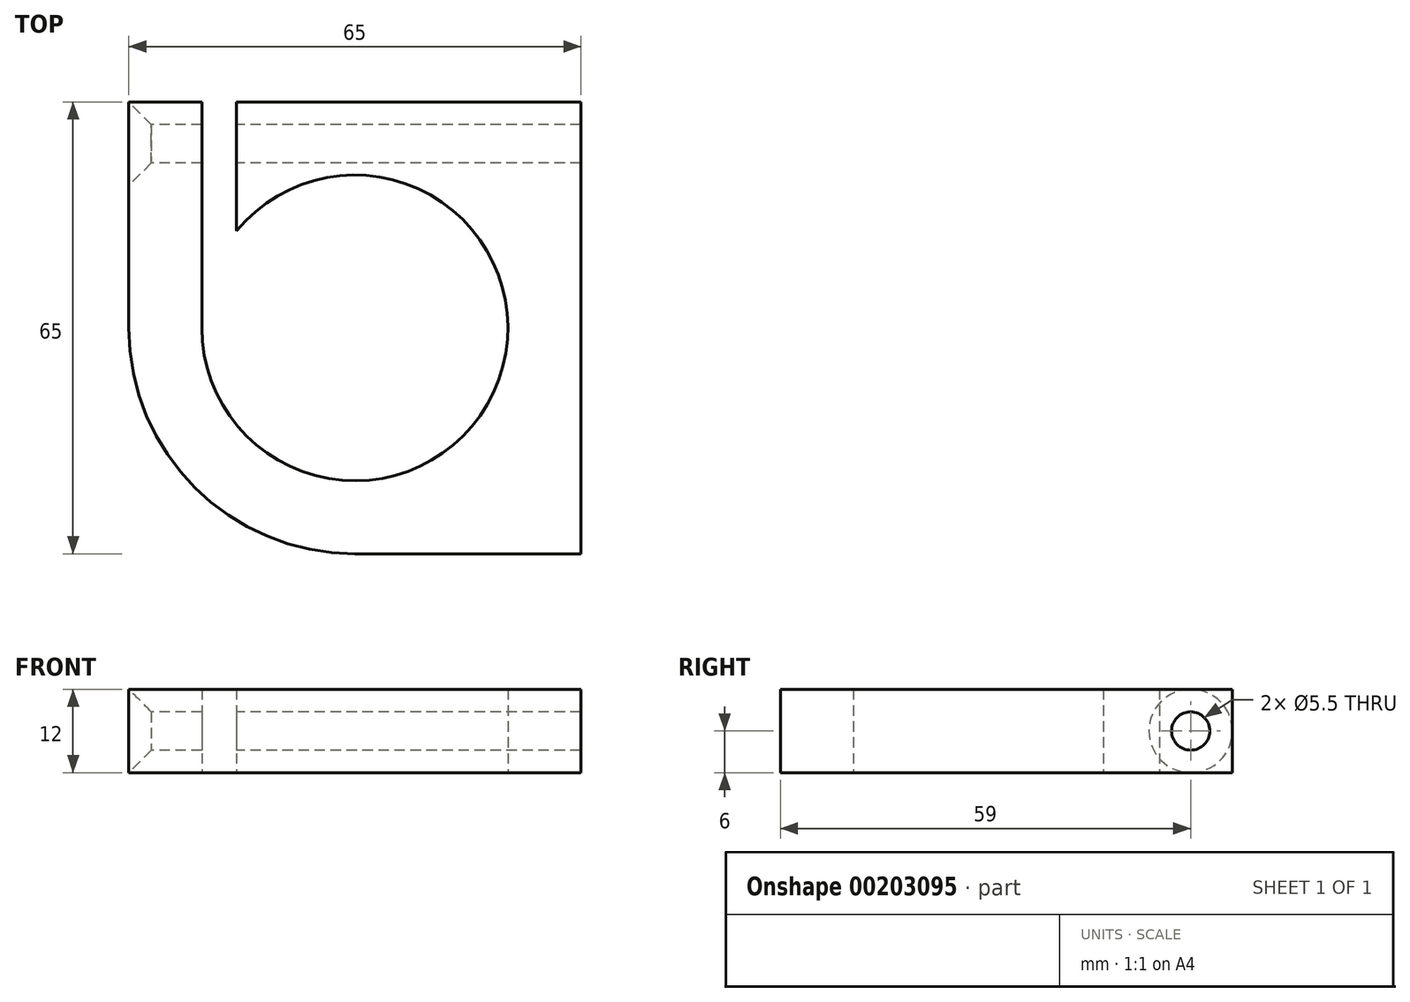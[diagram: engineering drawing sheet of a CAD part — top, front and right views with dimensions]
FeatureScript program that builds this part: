
annotation { "Feature Type Name" : "Feature", "Feature Type Description" : "" }
export const myFeature = defineFeature(function(context is Context, id is Id, definition is map)
    precondition{}
    {
        {
            var Q0;
            Q0=qCreatedBy(makeId("Top.planeOp"),FACE);
            var sketch = newSketch(context, id + "F0", { "sketchPlane" : qUnion([Q0])});
            skArc(sketch, "E0", {"start": v(-22, 0) * mm, "mid": v(20.71, -7.42) * mm, "end": v(-17, 13.96) * mm});
            skArc(sketch, "E1", {"start": v(-32.5, 0) * mm, "mid": v(-22.98, -22.98) * mm, "end": v(0, -32.5) * mm});
            skLineSegment(sketch, "E2", {"start": v(0, -32.5) * mm, "end": v(32.5, -32.5) * mm});
            skLineSegment(sketch, "E3", {"start": v(0, 32.5) * mm, "end": v(32.5, 32.5) * mm});
            skLineSegment(sketch, "E4", {"start": v(32.5, 32.5) * mm, "end": v(32.5, -32.5) * mm});
            skLineSegment(sketch, "E5", {"start": v(0, 32.5) * mm, "end": v(-17, 32.5) * mm});
            skLineSegment(sketch, "E6", {"start": v(-32.5, 0) * mm, "end": v(-32.5, 32.5) * mm});
            skLineSegment(sketch, "E7", {"start": v(-22, 0) * mm, "end": v(-22, 32.5) * mm});
            skLineSegment(sketch, "E8", {"start": v(-17, 13.96) * mm, "end": v(-17, 32.5) * mm});
            skLineSegment(sketch, "E9.trimOffspring", {"start": v(-22, 32.5) * mm, "end": v(-32.5, 32.5) * mm});
            skSolve(sketch);
        }
        {
            var Q0;
            Q0=makeQuery(id+"F0.imprint","IMPRINT",FACE,{"disambiguationData":[TD([[makeQuery(id+"F0.imprint","IMPRINT",EDGE,{"derivedFrom":sQuery(id+"F0.wireOp",EDGE,"E0")}),-1.0]])]});
            extrude(context, id + "F1", {"entities" : qUnion([Q0]), "offsetDistance" : 25 * mm, "depth" : 12 * mm});
        }
        {
            var Q0;
            Q0=makeQuery(id+"F1.opExtrude","SWEPT_FACE",FACE,{"disambiguationData":[OSD([sQuery(id+"F0.wireOp",EDGE,"E6")])]});
            var sketch = newSketch(context, id + "F2", { "sketchPlane" : qUnion([Q0])});
            skLineSegment(sketch, "E10", {"start": v(-32.5, 6) * mm, "end": v(-20.5, 6) * mm, "construction": true});
            skLineSegment(sketch, "E11", {"start": v(-26.5, 6) * mm, "end": v(-26.5, 10.93) * mm, "construction": true});
            skCircle(sketch, "E12", {"center": v(-26.5, 6) * mm, "radius": 2.75 * mm});
            skSolve(sketch);
        }
        {
            var Q0;
            Q0=sQuery(id+"F2.wireOp",VERTEX,"E12.center");
            var Q1;
            Q1=makeQuery(id+"F1.opExtrude","SWEPT_BODY",BODY,{"disambiguationData":[OSD([sQuery(id+"F0.wireOp",EDGE,"E0"),sQuery(id+"F0.wireOp",EDGE,"E1"),sQuery(id+"F0.wireOp",EDGE,"E2"),sQuery(id+"F0.wireOp",EDGE,"E3"),sQuery(id+"F0.wireOp",EDGE,"E4"),sQuery(id+"F0.wireOp",EDGE,"E5"),sQuery(id+"F0.wireOp",EDGE,"E6"),sQuery(id+"F0.wireOp",EDGE,"E7"),sQuery(id+"F0.wireOp",EDGE,"E8"),sQuery(id+"F0.wireOp",EDGE,"E9.trimOffspring")])]});
            hole(context, id + "F3", {"style" : HoleStyle.C_SINK, "endStyle" : HoleEndStyle.THROUGH, "holeDiameter" : 5.5 * mm, "cSinkDiameter" : 12 * mm, "cSinkAngle" : 90 * degree, "majorDiameter" : 5 * mm, "locations" : qUnion([Q0]), "scope" : qUnion([Q1]), "isTappedThrough" : true, "tappedDepth" : 12 * mm, "tapClearance" : 3});
        }
    });
